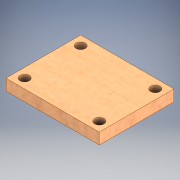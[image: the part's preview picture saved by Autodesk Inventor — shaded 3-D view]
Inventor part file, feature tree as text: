
AUTODESK INVENTOR PART (.ipt)
format: ipt  version: 2020 (Build 240168000, 168)  size: 130,560 bytes
history: native  units: mm
features: extrude x1, sketch x1
ambient origin geometry x8: Origin, YZ Plane, XZ Plane, XY Plane, X Axis, Y Axis, Z Axis, Center Point
bodies: Solide1 (feature_tree)
feature tree (2):
  extrude  "Extrusion1"  Depth=50.0mm
  sketch  "Esquisse1"
